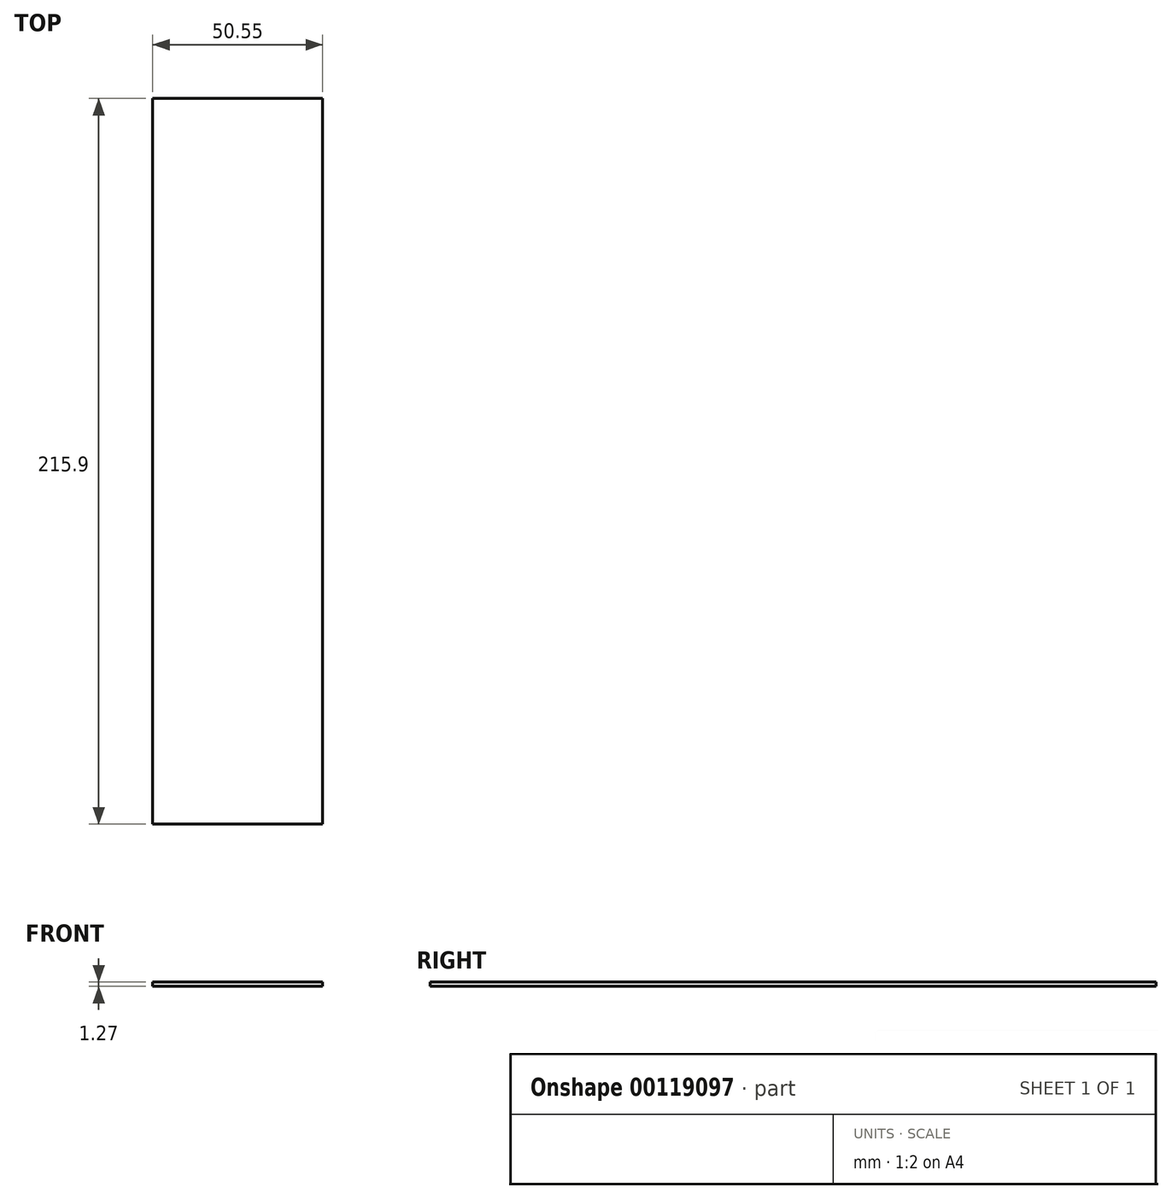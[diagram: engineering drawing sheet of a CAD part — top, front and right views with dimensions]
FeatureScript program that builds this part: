
annotation { "Feature Type Name" : "Feature", "Feature Type Description" : "" }
export const myFeature = defineFeature(function(context is Context, id is Id, definition is map)
    precondition{}
    {
        {
            var Q0;
            Q0=qCreatedBy(makeId("Top.planeOp"),FACE);
            var sketch = newSketch(context, id + "F0", { "sketchPlane" : qUnion([Q0])});
            skLineSegment(sketch, "E0.bottom", {"start": v(0, 0) * mm, "end": v(-50.55, 0) * mm});
            skLineSegment(sketch, "E0.top", {"start": v(0, -215.9) * mm, "end": v(-50.55, -215.9) * mm});
            skLineSegment(sketch, "E0.left", {"start": v(0, 0) * mm, "end": v(0, -215.9) * mm});
            skLineSegment(sketch, "E0.right", {"start": v(-50.55, 0) * mm, "end": v(-50.55, -215.9) * mm});
            skSolve(sketch);
        }
        {
            var Q0;
            Q0=makeQuery(id+"F0.imprint","IMPRINT",FACE,{"disambiguationData":[TD([[makeQuery(id+"F0.imprint","IMPRINT",EDGE,{"derivedFrom":sQuery(id+"F0.wireOp",EDGE,"E0.bottom")}),1.0]])]});
            extrude(context, id + "F1", {"entities" : qUnion([Q0]), "depth" : 1.27 * mm});
        }
    });
